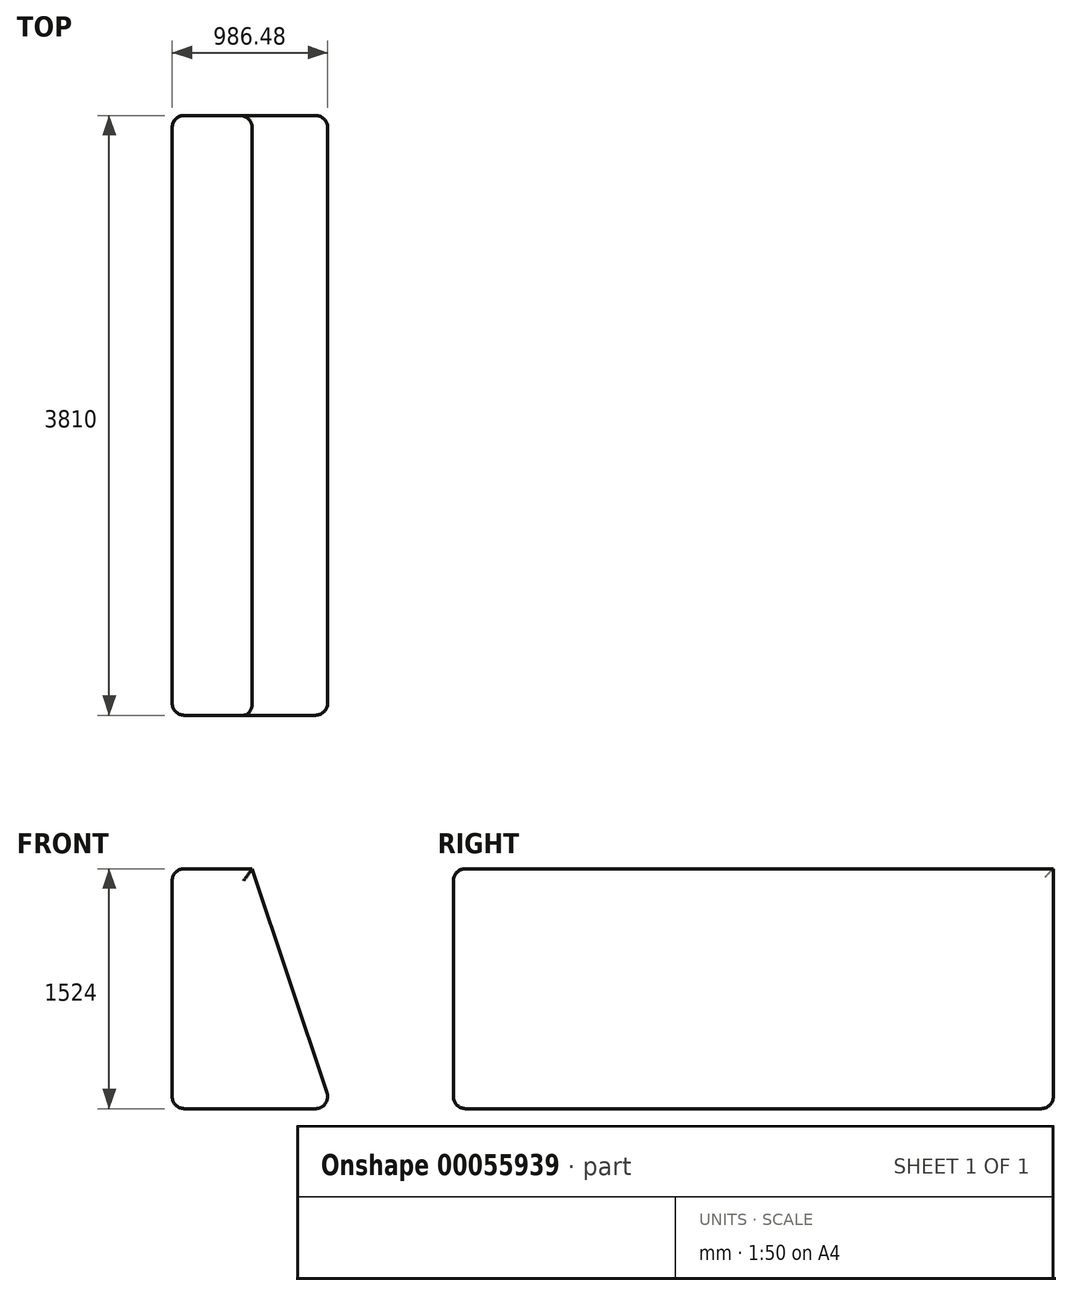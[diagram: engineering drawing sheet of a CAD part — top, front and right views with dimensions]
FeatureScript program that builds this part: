
annotation { "Feature Type Name" : "Feature", "Feature Type Description" : "" }
export const myFeature = defineFeature(function(context is Context, id is Id, definition is map)
    precondition{}
    {
        {
            var Q0;
            Q0=qCreatedBy(makeId("Front.planeOp"),FACE);
            var sketch = newSketch(context, id + "F0", { "sketchPlane" : qUnion([Q0])});
            skLineSegment(sketch, "E0", {"start": v(-2333.42, 1422.86) * mm, "end": v(-1825.42, 1422.86) * mm});
            skLineSegment(sketch, "E1", {"start": v(-2333.42, 1422.86) * mm, "end": v(-2333.42, -101.14) * mm});
            skLineSegment(sketch, "E2", {"start": v(-2333.42, -101.14) * mm, "end": v(-1317.42, -101.14) * mm});
            skLineSegment(sketch, "E3", {"start": v(-1825.42, 1422.86) * mm, "end": v(-1317.42, -101.14) * mm});
            skSolve(sketch);
        }
        {
            var Q0;
            Q0=makeQuery(id+"F0.imprint","IMPRINT",FACE,{"disambiguationData":[TD([[makeQuery(id+"F0.imprint","IMPRINT",EDGE,{"derivedFrom":sQuery(id+"F0.wireOp",EDGE,"E0")}),-1.0]])]});
            extrude(context, id + "F1", {"entities" : qUnion([Q0]), "depth" : 3810 * mm});
        }
        {
            var Q0;
            Q0=makeQuery(id+"F1.opExtrude","CAP_EDGE",EDGE,{"disambiguationData":[OSD([sQuery(id+"F0.wireOp",EDGE,"E3")])],"isStart":false});
            var Q1;
            Q1=makeQuery(id+"F1.opExtrude","CAP_EDGE",EDGE,{"disambiguationData":[OSD([sQuery(id+"F0.wireOp",EDGE,"E3")])],"isStart":true});
            var Q2;
            Q2=makeQuery(id+"F1.opExtrude","CAP_FACE",FACE,{"disambiguationData":[OSD([sQuery(id+"F0.wireOp",EDGE,"E0"),sQuery(id+"F0.wireOp",EDGE,"E1"),sQuery(id+"F0.wireOp",EDGE,"E2"),sQuery(id+"F0.wireOp",EDGE,"E3")])],"isStart":false});
            var Q3;
            Q3=makeQuery(id+"F1.opExtrude","CAP_EDGE",EDGE,{"disambiguationData":[OSD([sQuery(id+"F0.wireOp",EDGE,"E1")])],"isStart":false});
            var Q4;
            Q4=makeQuery(id+"F1.opExtrude","CAP_EDGE",EDGE,{"disambiguationData":[OSD([sQuery(id+"F0.wireOp",EDGE,"E0")])],"isStart":false});
            var Q5;
            Q5=makeQuery(id+"F1.opExtrude","SWEPT_FACE",FACE,{"disambiguationData":[OSD([sQuery(id+"F0.wireOp",EDGE,"E1")])]});
            var Q6;
            Q6=makeQuery(id+"F1.opExtrude","SWEPT_FACE",FACE,{"disambiguationData":[OSD([sQuery(id+"F0.wireOp",EDGE,"E2")])]});
            var Q7;
            Q7=makeQuery(id+"F1.opExtrude","SWEPT_EDGE",EDGE,{"disambiguationData":[OSD([sQuery(id+"F0.wireOp",EDGE,"E2"),sQuery(id+"F0.wireOp",EDGE,"E3")])]});
            var Q8;
            Q8=makeQuery(id+"F1.opExtrude","CAP_EDGE",EDGE,{"disambiguationData":[OSD([sQuery(id+"F0.wireOp",EDGE,"E2")])],"isStart":false});
            fillet(context, id + "F2", {"entities" : qUnion([Q0, Q1, Q2, Q3, Q4, Q5, Q6, Q7, Q8]), "radius" : 76.2 * mm, "tangentPropagation" : true, "allowEdgeOverflow" : false});
        }
    });
